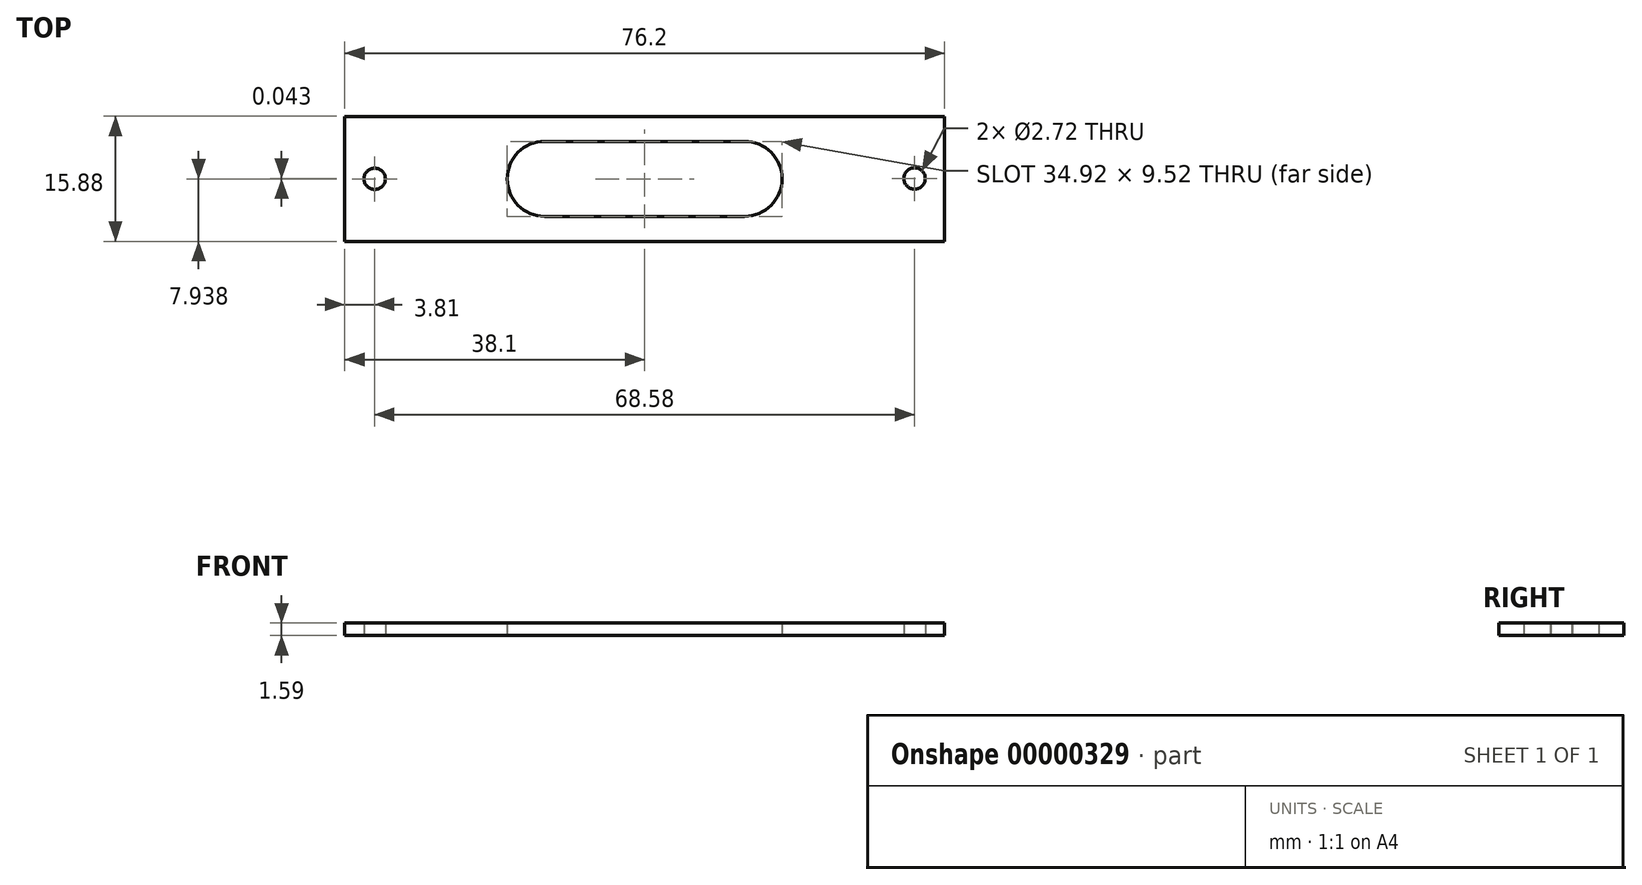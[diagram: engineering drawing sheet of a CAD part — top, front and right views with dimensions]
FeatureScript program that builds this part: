
annotation { "Feature Type Name" : "Feature", "Feature Type Description" : "" }
export const myFeature = defineFeature(function(context is Context, id is Id, definition is map)
    precondition{}
    {
        {
            var Q0;
            Q0=qCreatedBy(makeId("Top.planeOp"),FACE);
            var sketch = newSketch(context, id + "F0", { "sketchPlane" : qUnion([Q0])});
            skLineSegment(sketch, "E0.bottom", {"start": v(0, 0) * mm, "end": v(76.2, 0) * mm});
            skLineSegment(sketch, "E0.top", {"start": v(0, 15.88) * mm, "end": v(76.2, 15.88) * mm});
            skLineSegment(sketch, "E0.left", {"start": v(0, 0) * mm, "end": v(0, 15.88) * mm});
            skLineSegment(sketch, "E0.right", {"start": v(76.2, 0) * mm, "end": v(76.2, 15.88) * mm});
            skArc(sketch, "E1", {"start": v(25.4, 12.7) * mm, "mid": v(20.64, 7.94) * mm, "end": v(25.4, 3.17) * mm});
            skArc(sketch, "E2", {"start": v(50.8, 3.18) * mm, "mid": v(55.56, 7.94) * mm, "end": v(50.8, 12.7) * mm});
            skLineSegment(sketch, "E3", {"start": v(25.4, 12.7) * mm, "end": v(50.8, 12.7) * mm});
            skLineSegment(sketch, "E4", {"start": v(50.8, 3.18) * mm, "end": v(25.4, 3.17) * mm});
            skCircle(sketch, "E5", {"center": v(3.8, 7.94) * mm, "radius": 1.36 * mm});
            skCircle(sketch, "E6", {"center": v(72.4, 7.98) * mm, "radius": 1.36 * mm});
            skLineSegment(sketch, "E7", {"start": v(0, 7.94) * mm, "end": v(3.8, 7.94) * mm, "construction": true});
            skLineSegment(sketch, "E8", {"start": v(72.4, 7.98) * mm, "end": v(76.2, 7.98) * mm, "construction": true});
            skSolve(sketch);
        }
        {
            var Q0;
            Q0=makeQuery(id+"F0.imprint","IMPRINT",FACE,{"disambiguationData":[TD([[makeQuery(id+"F0.imprint","IMPRINT",EDGE,{"derivedFrom":sQuery(id+"F0.wireOp",EDGE,"E0.bottom")}),1.0]])]});
            extrude(context, id + "F1", {"entities" : qUnion([Q0]), "depth" : 1.59 * mm});
        }
    });
